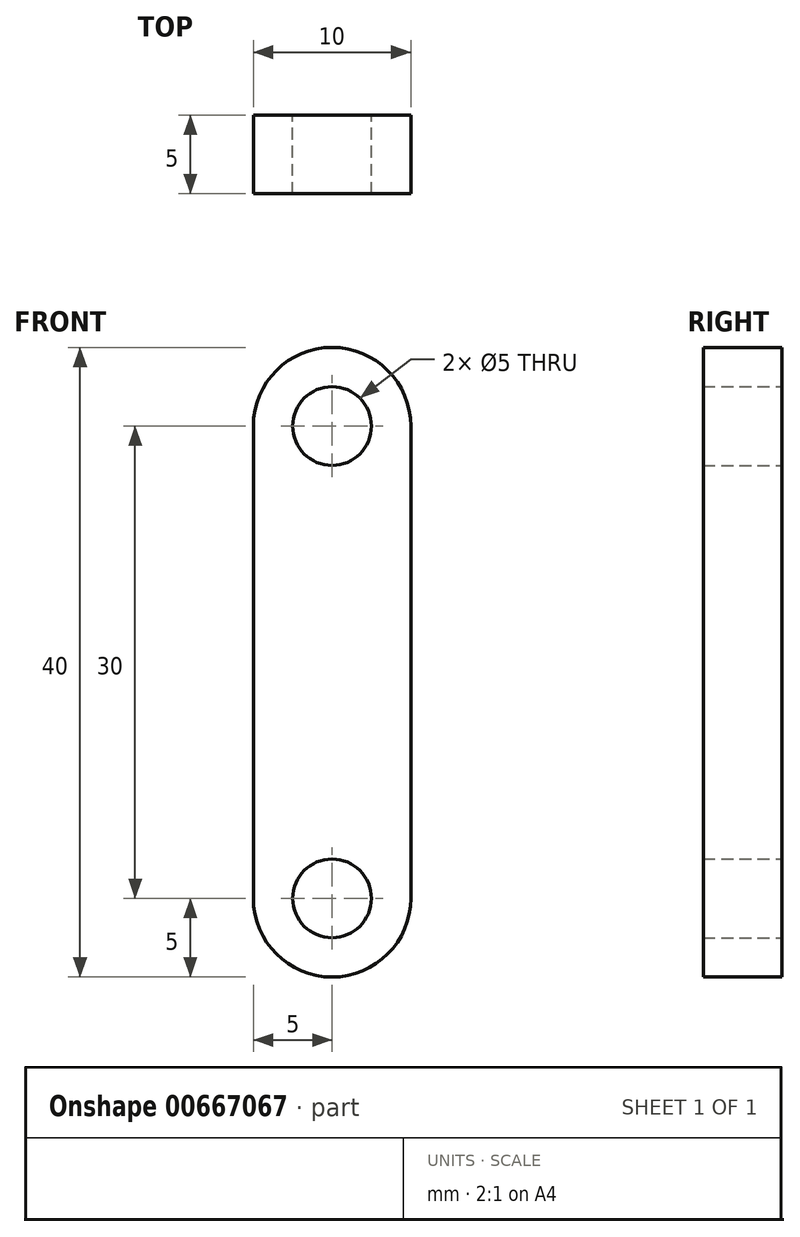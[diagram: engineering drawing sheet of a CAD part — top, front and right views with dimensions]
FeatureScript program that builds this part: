
annotation { "Feature Type Name" : "Feature", "Feature Type Description" : "" }
export const myFeature = defineFeature(function(context is Context, id is Id, definition is map)
    precondition{}
    {
        {
            var Q0;
            Q0=qCreatedBy(makeId("Front.planeOp"),FACE);
            var sketch = newSketch(context, id + "F0", { "sketchPlane" : qUnion([Q0])});
            skCircle(sketch, "E0", {"center": v(0, 0) * mm, "radius": 5 * mm});
            skCircle(sketch, "E1", {"center": v(0, 30) * mm, "radius": 5 * mm});
            skCircle(sketch, "E2", {"center": v(0, 30) * mm, "radius": 2.5 * mm});
            skCircle(sketch, "E3", {"center": v(0, 0) * mm, "radius": 2.5 * mm});
            skLineSegment(sketch, "E4", {"start": v(-5, 30) * mm, "end": v(-5, 0) * mm});
            skLineSegment(sketch, "E5", {"start": v(5, 30) * mm, "end": v(5, 0) * mm});
            skSolve(sketch);
        }
        {
            var Q0;
            {var subQ0=sQuery(id+"F0.wireOp",EDGE,"E4");Q0=makeQuery(id+"F0.imprint","IMPRINT",FACE,{"disambiguationData":[TD([[makeQuery(id+"F0.imprint","IMPRINT",EDGE,{"derivedFrom":subQ0}),1.0]])]});}
            var Q1;
            Q1=makeQuery(id+"F0.imprint","IMPRINT",FACE,{"disambiguationData":[TD([[makeQuery(id+"F0.imprint","IMPRINT",EDGE,{"derivedFrom":sQuery(id+"F0.wireOp",EDGE,"E2")}),-1.0]])]});
            var Q2;
            Q2=makeQuery(id+"F0.imprint","IMPRINT",FACE,{"disambiguationData":[TD([[makeQuery(id+"F0.imprint","IMPRINT",EDGE,{"derivedFrom":sQuery(id+"F0.wireOp",EDGE,"E3")}),-1.0]])]});
            extrude(context, id + "F1", {"entities" : qUnion([Q0, Q1, Q2]), "endBound" : BoundingType.SYMMETRIC, "depth" : 5 * mm, "offsetDistance" : 25 * mm});
        }
    });
